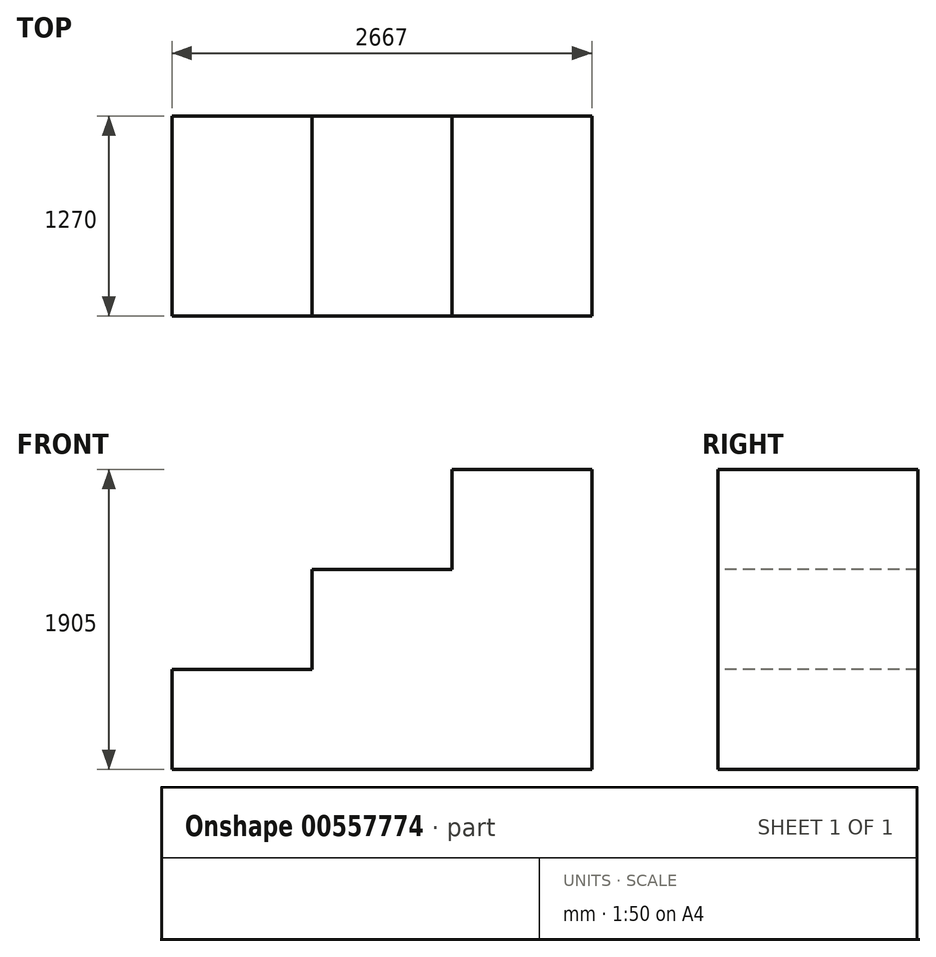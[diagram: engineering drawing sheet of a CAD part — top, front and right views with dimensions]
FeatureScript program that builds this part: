
annotation { "Feature Type Name" : "Feature", "Feature Type Description" : "" }
export const myFeature = defineFeature(function(context is Context, id is Id, definition is map)
    precondition{}
    {
        {
            var Q0;
            Q0=qCreatedBy(makeId("Front.planeOp"),FACE);
            var sketch = newSketch(context, id + "F0", { "sketchPlane" : qUnion([Q0])});
            skLineSegment(sketch, "E0", {"start": v(-76.19, 1889.37) * mm, "end": v(-76.19, -15.63) * mm});
            skLineSegment(sketch, "E1", {"start": v(-76.19, -15.63) * mm, "end": v(2590.81, -15.63) * mm});
            skLineSegment(sketch, "E2", {"start": v(2590.81, -15.63) * mm, "end": v(2590.81, 1889.37) * mm});
            skLineSegment(sketch, "E3", {"start": v(2590.81, 1889.37) * mm, "end": v(-76.19, 1889.37) * mm});
            skSolve(sketch);
        }
        {
            var Q0;
            Q0=makeQuery(id+"F0.imprint","IMPRINT",FACE,{"disambiguationData":[TD([[makeQuery(id+"F0.imprint","IMPRINT",EDGE,{"derivedFrom":sQuery(id+"F0.wireOp",EDGE,"E0")}),1.0]])]});
            extrude(context, id + "F1", {"entities" : qUnion([Q0]), "depth" : 1270 * mm, "offsetDistance" : 25.4 * mm});
        }
        {
            var Q0;
            Q0=makeQuery(id+"F1.opExtrude","CAP_FACE",FACE,{"disambiguationData":[OSD([sQuery(id+"F0.wireOp",EDGE,"E0"),sQuery(id+"F0.wireOp",EDGE,"E1"),sQuery(id+"F0.wireOp",EDGE,"E2"),sQuery(id+"F0.wireOp",EDGE,"E3")])],"isStart":false});
            var sketch = newSketch(context, id + "F2", { "sketchPlane" : qUnion([Q0])});
            skLineSegment(sketch, "E4", {"start": v(-76.19, -15.63) * mm, "end": v(-76.19, 619.37) * mm});
            skLineSegment(sketch, "E5", {"start": v(-76.19, 619.37) * mm, "end": v(812.81, 619.37) * mm});
            skLineSegment(sketch, "E6", {"start": v(812.81, 619.37) * mm, "end": v(812.81, 1254.37) * mm});
            skLineSegment(sketch, "E7", {"start": v(812.81, 1254.37) * mm, "end": v(1701.81, 1254.37) * mm});
            skLineSegment(sketch, "E8", {"start": v(1701.81, 1254.37) * mm, "end": v(1701.81, 1889.37) * mm});
            skSolve(sketch);
        }
        {
            var Q0;
            {var subQ1=sQuery(id+"F2.wireOp",EDGE,"E5");Q0=makeQuery(id+"F2.imprint","IMPRINT",FACE,{"disambiguationData":[TD([[makeQuery(id+"F2.imprint","IMPRINT",EDGE,{"derivedFrom":subQ1}),1.0]])]});}
            extrude(context, id + "F3", {"entities" : qUnion([Q0]), "operationType" : NewBodyOperationType.REMOVE, "endBound" : BoundingType.THROUGH_ALL, "oppositeDirection" : true, "depth" : 25.4 * mm, "offsetDistance" : 25.4 * mm});
        }
    });
